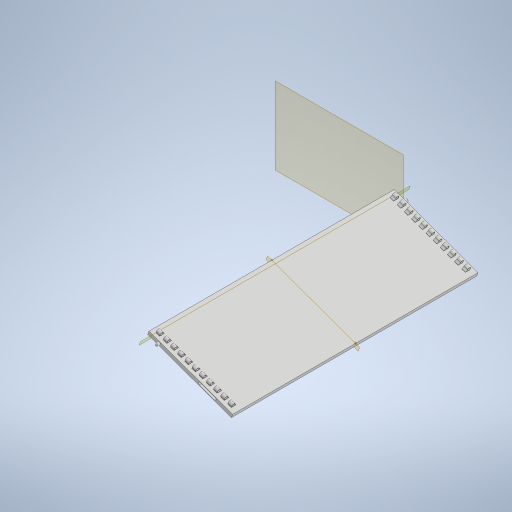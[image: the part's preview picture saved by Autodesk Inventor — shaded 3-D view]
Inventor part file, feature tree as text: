
AUTODESK INVENTOR PART (.ipt)
format: ipt  version: 2023 (Build 270158030, 158C)  size: 552,448 bytes
history: native  units: mm
features: other x11, extrude x4, sketch x4, plane x3, reference x3, mirror x2, fillet x1, pattern_linear x1
ambient origin geometry x8: Origin, YZ Plane, XZ Plane, XY Plane, X Axis, Y Axis, Z Axis, Center Point
bodies: Body1 (feature_tree), Body2 (feature_tree), Body3 (feature_tree)
feature tree (29):
  other  "bed-base"
  plane  "Work Plane4"
  extrude  "Extrusion1"  Depth=30.0mm
  extrude  "Extrusion2"  Depth=10.0mm
  extrude  "Extrusion3"  Depth=22.0mm
  fillet  "Fillet1"  Radius=4.0mm
  plane  "Work Plane5"
  extrude  "Extrusion4"  TaperAngle=0.0deg  [1 undecoded]
  pattern_linear  "Rectangular Pattern1"  Count1=3 Spacing1=0.0mm
  other  "Work Point1"
  other  "Work Point2"
  other  "Work Point3"
  plane  "Work Plane6"
  mirror  "Mirror1"
  mirror  "Mirror2"
  sketch  "Sketch3"  dims[d1=700.0mm d2=30.0mm]
  reference  "Reference2"
  sketch  "Sketch4"  dims[d3=5.0mm d4=10.0mm]
  reference  "Reference3"
  sketch  "Sketch5"  dims[d5=1930.0mm d6=0.0mm d7=22.0mm d8=4.0mm]
  other  "location-pin"
  sketch  "Sketch6"  dims[d9=4.0mm d11=0.0mm d12=30.0mm d13=0.0mm d14=20.0mm d15=15.0mm d16=15.0mm d17=90.0mm d18=25.0mm d19=0.0mm d20=6.0mm d21=120.0mm d22=-30.0mm d23=2.5mm d24=11.0mm d25=25.0mm d26=3.0mm d27=4.0mm d28=6.0mm d29=3.0mm d30=20.0mm d31=30.0mm d32=0.0mm d33=110.0mm d35=60.0mm]
  reference  "Reference4"
  other  "hinge"
  other  "<userpath>\Documents\0004-inventor\3D-CAD-main\primary-engineer-bench.iam"
  other  "primary-engineer-bench.iam"
  other  "bench-end-peice_MIR:1"
  other  "bench-end-peice:1"
  other  "back-flaps-3:1"
note: 1 required parameter value undecoded (feature->parameter linkage not recoverable at this tier; creation-order binding heuristic only, values carry confidence <= 0.55)
